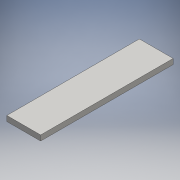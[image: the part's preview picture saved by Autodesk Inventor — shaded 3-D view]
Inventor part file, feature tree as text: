
AUTODESK INVENTOR PART (.ipt)
format: ipt  version: 2016 SP1 (Build 200210100, 210)  size: 88,576 bytes
history: native  units: mm
features: extrude x1, sketch x1
ambient origin geometry x8: Origin, YZ Plane, XZ Plane, XY Plane, X Axis, Y Axis, Z Axis, Center Point
bodies: Solid1 (feature_tree)
feature tree (2):
  extrude  "Extrusion1"  Depth=200.0mm
  sketch  "Sketch1"  dims[d0=51.0mm d1=200.0mm d2=100.0mm d3=25.5mm d4=8.0mm d5=0.0mm]
